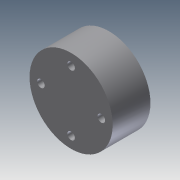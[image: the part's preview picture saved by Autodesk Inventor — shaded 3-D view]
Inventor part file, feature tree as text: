
AUTODESK INVENTOR PART (.ipt)
format: ipt  version: 2011 (Build 150239000, 239)  size: 88,576 bytes
history: native  units: in
note: dims shown in document units (in); Inventor stores cm internally (conversion verified against a paired STEP export)
features: extrude x2, sketch x2
ambient origin geometry x8: Origin, YZ Plane, XZ Plane, XY Plane, X Axis, Y Axis, Z Axis, Center Point
bodies: Solid1 (feature_tree)
feature tree (4):
  extrude  "Extrusion1"  Depth=0.3937in TaperAngle=0.0deg
  extrude  "Extrusion2"  Depth=0.0787in
  sketch  "Sketch1"  dims[d0=0.8661in d1=0.3937in d2=0.0in]
  sketch  "Sketch2"  dims[d3=0.6299in d4=0.0787in d5=0.0787in d6=0.0787in d7=0.0787in d8=0.3937in d9=0.0in]
